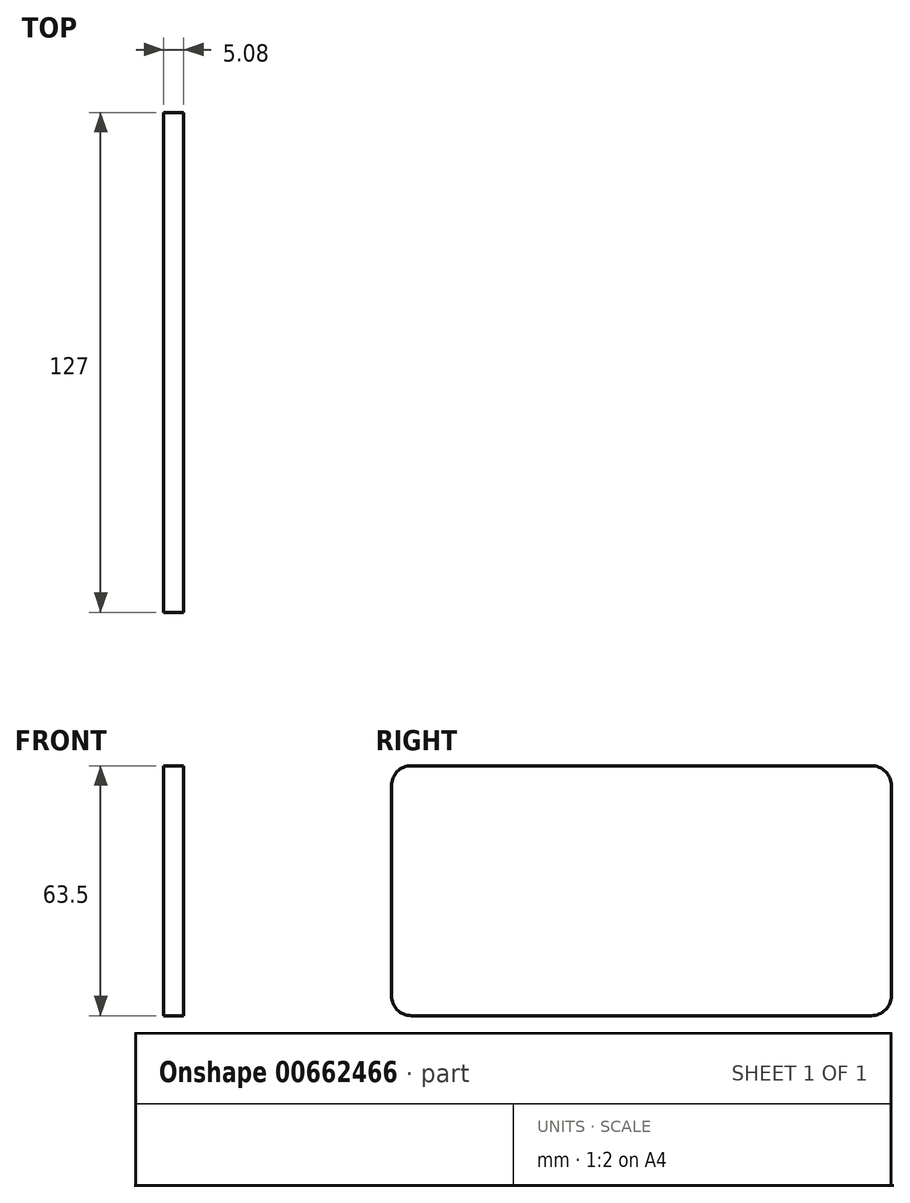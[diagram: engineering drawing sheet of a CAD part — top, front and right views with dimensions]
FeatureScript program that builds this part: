
annotation { "Feature Type Name" : "Feature", "Feature Type Description" : "" }
export const myFeature = defineFeature(function(context is Context, id is Id, definition is map)
    precondition{}
    {
        {
            var Q0;
            Q0=qCreatedBy(makeId("Right.planeOp"),FACE);
            var sketch = newSketch(context, id + "F0", { "sketchPlane" : qUnion([Q0])});
            skLineSegment(sketch, "E0.bottom", {"start": v(-63.5, 63.5) * mm, "end": v(63.5, 63.5) * mm});
            skLineSegment(sketch, "E0.top", {"start": v(-63.5, 0) * mm, "end": v(63.5, 0) * mm});
            skLineSegment(sketch, "E0.left", {"start": v(-63.5, 63.5) * mm, "end": v(-63.5, 0) * mm});
            skLineSegment(sketch, "E1", {"start": v(0, 140.65) * mm, "end": v(0, 103.5) * mm, "construction": true});
            skLineSegment(sketch, "E2", {"start": v(63.5, 0) * mm, "end": v(63.5, 63.5) * mm});
            skSolve(sketch);
        }
        {
            var Q0;
            Q0=makeQuery(id+"F0.imprint","IMPRINT",FACE,{"disambiguationData":[TD([[makeQuery(id+"F0.imprint","IMPRINT",EDGE,{"derivedFrom":sQuery(id+"F0.wireOp",EDGE,"E0.bottom")}),-1.0]])]});
            extrude(context, id + "F1", {"entities" : qUnion([Q0]), "depth" : 5.08 * mm, "offsetDistance" : 25.4 * mm});
        }
        {
            var Q0;
            Q0=makeQuery(id+"F1.opExtrude","SWEPT_EDGE",EDGE,{"disambiguationData":[OSD([sQuery(id+"F0.wireOp",EDGE,"E0.bottom"),sQuery(id+"F0.wireOp",EDGE,"E0.left")])]});
            var Q1;
            Q1=makeQuery(id+"F1.opExtrude","SWEPT_EDGE",EDGE,{"disambiguationData":[OSD([sQuery(id+"F0.wireOp",EDGE,"E0.bottom"),sQuery(id+"F0.wireOp",EDGE,"E2")])]});
            var Q2;
            Q2=makeQuery(id+"F1.opExtrude","SWEPT_EDGE",EDGE,{"disambiguationData":[OSD([sQuery(id+"F0.wireOp",EDGE,"E0.top"),sQuery(id+"F0.wireOp",EDGE,"E0.left")])]});
            var Q3;
            Q3=makeQuery(id+"F1.opExtrude","SWEPT_EDGE",EDGE,{"disambiguationData":[OSD([sQuery(id+"F0.wireOp",EDGE,"E0.top"),sQuery(id+"F0.wireOp",EDGE,"E2")])]});
            fillet(context, id + "F2", {"entities" : qUnion([Q0, Q1, Q2, Q3]), "radius" : 5.08 * mm, "tangentPropagation" : true, "allowEdgeOverflow" : false});
        }
    });
